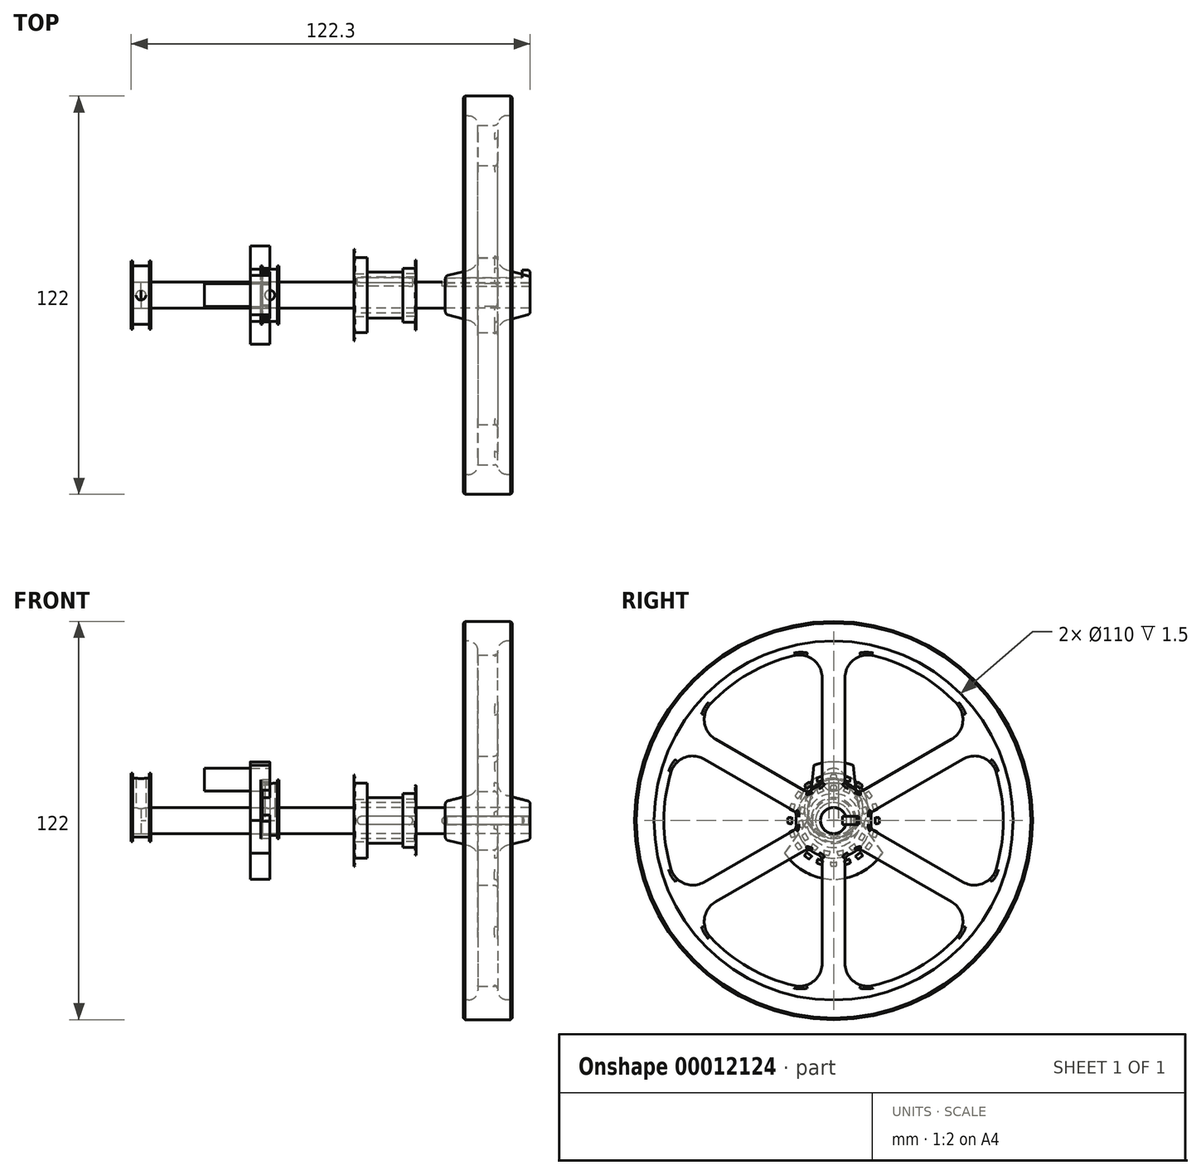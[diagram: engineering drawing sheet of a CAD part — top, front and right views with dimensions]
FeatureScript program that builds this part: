
annotation { "Feature Type Name" : "Feature", "Feature Type Description" : "" }
export const myFeature = defineFeature(function(context is Context, id is Id, definition is map)
    precondition{}
    {
        {
            var Q0;
            Q0=qCreatedBy(makeId("Right.planeOp"),FACE);
            var sketch = newSketch(context, id + "F0", { "sketchPlane" : qUnion([Q0])});
            skCircle(sketch, "E0", {"center": v(0, 0) * mm, "radius": 4 * mm});
            skSolve(sketch);
        }
        {
            var Q0;
            Q0=makeQuery(id+"F0.imprint","IMPRINT",FACE,{"disambiguationData":[TD([[makeQuery(id+"F0.imprint","IMPRINT",EDGE,{"derivedFrom":sQuery(id+"F0.wireOp",EDGE,"E0")}),1.0]])]});
            extrude(context, id + "F1", {"entities" : qUnion([Q0]), "oppositeDirection" : true, "depth" : 39.5 * mm});
        }
        {
            var Q0;
            Q0=makeQuery(id+"F1.opExtrude","CAP_FACE",FACE,{"disambiguationData":[OSD([sQuery(id+"F0.wireOp",EDGE,"E0")])],"isStart":true});
            var sketch = newSketch(context, id + "F2", { "sketchPlane" : qUnion([Q0])});
            skCircle(sketch, "E1", {"center": v(0, 0) * mm, "radius": 18 * mm});
            skLineSegment(sketch, "E2", {"start": v(0, 0) * mm, "end": v(0, 12.5) * mm, "construction": true});
            skCircle(sketch, "E3", {"center": v(0, 12.5) * mm, "radius": 3.5 * mm});
            skLineSegment(sketch, "E4.0", {"start": v(6, 0) * mm, "end": v(6, 16.97) * mm, "construction": true});
            skLineSegment(sketch, "E5", {"start": v(0, 0) * mm, "end": v(8, 0) * mm, "construction": true});
            skLineSegment(sketch, "E6", {"start": v(0, 0) * mm, "end": v(15, 0) * mm, "construction": true});
            skLineSegment(sketch, "E7", {"start": v(15, 0) * mm, "end": v(15, -9.95) * mm, "construction": true});
            skLineSegment(sketch, "E8", {"start": v(6, 16.97) * mm, "end": v(8, 0) * mm});
            skLineSegment(sketch, "E9", {"start": v(8, 0) * mm, "end": v(15, -9.95) * mm});
            skLineSegment(sketch, "E10.0.MirrorCS", {"start": v(-6, 16.97) * mm, "end": v(-8, 0) * mm});
            skLineSegment(sketch, "E11.0.MirrorCS", {"start": v(-8, 0) * mm, "end": v(-15, -9.95) * mm});
            skSolve(sketch);
        }
        {
            var Q0;
            Q0=makeQuery(id+"F2.imprint","IMPRINT",FACE,{"disambiguationData":[TD([[makeQuery(id+"F2.imprint","IMPRINT",EDGE,{"derivedFrom":sQuery(id+"F2.wireOp",EDGE,"E3")}),-1.0]])]});
            extrude(context, id + "F3", {"entities" : qUnion([Q0]), "oppositeDirection" : true, "depth" : 6 * mm});
        }
        {
            var Q0;
            Q0=makeQuery(id+"F2.imprint","IMPRINT",FACE,{"disambiguationData":[TD([[makeQuery(id+"F2.imprint","IMPRINT",EDGE,{"derivedFrom":sQuery(id+"F2.wireOp",EDGE,"E3")}),1.0]])]});
            extrude(context, id + "F4", {"entities" : qUnion([Q0]), "oppositeDirection" : true, "depth" : 20 * mm});
        }
        {
            var Q0;
            Q0=makeQuery(id+"F2.imprint","IMPRINT",FACE,{"disambiguationData":[TD([[makeQuery(id+"F2.imprint","IMPRINT",EDGE,{"derivedFrom":makeQuery(id+"F1.opExtrude","CAP_EDGE",EDGE,{"disambiguationData":[OSD([sQuery(id+"F0.wireOp",EDGE,"E0")])],"isStart":true})}),1.0]])]});
            extrude(context, id + "F5", {"entities" : qUnion([Q0]), "depth" : 79.8 * mm});
        }
        {
            var Q0;
            Q0=qCreatedBy(makeId("Front.planeOp"),FACE);
            cPlane(context, id + "F6", {"entities" : qUnion([Q0]), "cplaneType" : CPlaneType.OFFSET, "offset" : 4 * mm, "oppositeDirection" : true, "width" : 150 * mm, "height" : 150 * mm});
        }
        {
            var Q0;
            Q0=qCreatedBy(id+"F6.planeOp",FACE);
            var sketch = newSketch(context, id + "F7", { "sketchPlane" : qUnion([Q0])});
            skLineSegment(sketch, "E12.0", {"start": v(79.8, 4) * mm, "end": v(79.8, -4) * mm});
            skLineSegment(sketch, "E13", {"start": v(79.8, 0) * mm, "end": v(37.83, 0) * mm, "construction": true});
            skCircle(sketch, "E14", {"center": v(54.05, 0) * mm, "radius": 1.25 * mm});
            skCircle(sketch, "E15", {"center": v(42.55, 0) * mm, "radius": 1.25 * mm});
            skCircle(sketch, "E16", {"center": v(28.05, 0) * mm, "radius": 1.25 * mm});
            skLineSegment(sketch, "E17", {"start": v(54.05, -1.25) * mm, "end": v(79.8, -1.25) * mm});
            skLineSegment(sketch, "E18", {"start": v(42.55, 1.25) * mm, "end": v(28.05, 1.25) * mm});
            skLineSegment(sketch, "E19", {"start": v(42.55, -1.25) * mm, "end": v(28.05, -1.25) * mm});
            skLineSegment(sketch, "E20.0.MirrorCS", {"start": v(54.05, 1.25) * mm, "end": v(79.8, 1.25) * mm});
            skSolve(sketch);
        }
        {
            var Q0;
            {var subQ1=sQuery(id+"F7.wireOp",EDGE,"E17");Q0=makeQuery(id+"F7.imprint","IMPRINT",FACE,{"disambiguationData":[TD([[makeQuery(id+"F7.imprint","IMPRINT",EDGE,{"derivedFrom":subQ1}),1.0]])]});}
            var Q1;
            {var subQ0=sQuery(id+"F7.wireOp",EDGE,"E14");var subQ2=makeQuery(id+"F7.imprint","INTERSECT",VERTEX,{"derivedFrom":[subQ0,sQuery(id+"F7.wireOp",EDGE,"E17")]});Q1=makeQuery(id+"F7.imprint","IMPRINT",FACE,{"disambiguationData":[TD([[makeQuery(id+"F7.imprint","IMPRINT",EDGE,{"disambiguationData":[TD([[subQ2,1.0]])],"derivedFrom":subQ0}),1.0]])]});}
            var Q2;
            {var subQ1=sQuery(id+"F7.wireOp",EDGE,"E18");Q2=makeQuery(id+"F7.imprint","IMPRINT",FACE,{"disambiguationData":[TD([[makeQuery(id+"F7.imprint","IMPRINT",EDGE,{"derivedFrom":subQ1}),1.0]])]});}
            var Q3;
            {var subQ0=sQuery(id+"F7.wireOp",EDGE,"E15");var subQ2=makeQuery(id+"F7.imprint","INTERSECT",VERTEX,{"derivedFrom":[subQ0,sQuery(id+"F7.wireOp",EDGE,"E18")]});Q3=makeQuery(id+"F7.imprint","IMPRINT",FACE,{"disambiguationData":[TD([[makeQuery(id+"F7.imprint","IMPRINT",EDGE,{"disambiguationData":[TD([[subQ2,-1.0]])],"derivedFrom":subQ0}),1.0]])]});}
            var Q4;
            {var subQ0=sQuery(id+"F7.wireOp",EDGE,"E16");var subQ2=makeQuery(id+"F7.imprint","INTERSECT",VERTEX,{"derivedFrom":[subQ0,sQuery(id+"F7.wireOp",EDGE,"E18")]});Q4=makeQuery(id+"F7.imprint","IMPRINT",FACE,{"disambiguationData":[TD([[makeQuery(id+"F7.imprint","IMPRINT",EDGE,{"disambiguationData":[TD([[subQ2,-1.0]])],"derivedFrom":subQ0}),1.0]])]});}
            extrude(context, id + "F8", {"entities" : qUnion([Q0, Q1, Q2, Q3, Q4]), "operationType" : NewBodyOperationType.REMOVE, "depth" : 1.3 * mm});
        }
        {
            var Q0;
            Q0=qCreatedBy(makeId("Front.planeOp"),FACE);
            var sketch = newSketch(context, id + "F9", { "sketchPlane" : qUnion([Q0])});
            skLineSegment(sketch, "E21.0", {"start": v(79.8, 4) * mm, "end": v(79.8, -4) * mm});
            skLineSegment(sketch, "E22.bottom", {"start": v(79.8, 4) * mm, "end": v(53.8, 4) * mm});
            skLineSegment(sketch, "E22.top", {"start": v(79.8, 11.5) * mm, "end": v(53.8, 11.5) * mm});
            skLineSegment(sketch, "E22.left", {"start": v(79.8, 4) * mm, "end": v(79.8, 5.07) * mm});
            skLineSegment(sketch, "E22.right", {"start": v(53.8, 4) * mm, "end": v(53.8, 11.5) * mm});
            skLineSegment(sketch, "E23", {"start": v(66.8, 4) * mm, "end": v(66.8, 61) * mm, "construction": true});
            skLineSegment(sketch, "E24.bottom", {"start": v(74.3, 61) * mm, "end": v(59.3, 61) * mm});
            skLineSegment(sketch, "E24.top", {"start": v(74.3, 55) * mm, "end": v(72.8, 55) * mm});
            skLineSegment(sketch, "E24.left", {"start": v(74.3, 61) * mm, "end": v(74.3, 55) * mm});
            skLineSegment(sketch, "E24.right", {"start": v(59.3, 61) * mm, "end": v(59.3, 55) * mm});
            skLineSegment(sketch, "E25.bottom", {"start": v(60.8, 55) * mm, "end": v(59.3, 55) * mm});
            skLineSegment(sketch, "E25.top", {"start": v(69.8, 11.5) * mm, "end": v(63.8, 11.5) * mm});
            skLineSegment(sketch, "E25.left", {"start": v(69.8, 52) * mm, "end": v(69.8, 11.5) * mm});
            skLineSegment(sketch, "E25.right", {"start": v(63.8, 52) * mm, "end": v(63.8, 11.5) * mm});
            skArc(sketch, "E26.filletArc", {"start": v(72.8, 55) * mm, "mid": v(70.68, 54.12) * mm, "end": v(69.8, 52) * mm});
            skPoint(sketch, "E27.visualSharp", {"position": v(63.8, 55) * mm});
            skArc(sketch, "E27.filletArc", {"start": v(63.8, 52) * mm, "mid": v(62.92, 54.12) * mm, "end": v(60.8, 55) * mm});
            skLineSegment(sketch, "E28", {"start": v(79.05, 6.03) * mm, "end": v(72.81, 7.62) * mm});
            skLineSegment(sketch, "E29", {"start": v(69.8, 11.5) * mm, "end": v(69.8, 11.5) * mm});
            skPoint(sketch, "E30.visualSharp", {"position": v(69.8, 8.4) * mm});
            skArc(sketch, "E30.filletArc", {"start": v(69.8, 11.5) * mm, "mid": v(70.64, 9.05) * mm, "end": v(72.81, 7.62) * mm});
            skPoint(sketch, "E31.newPointB", {"position": v(79.8, 11.5) * mm});
            skArc(sketch, "E31.filletArc", {"start": v(79.8, 5.07) * mm, "mid": v(79.59, 5.68) * mm, "end": v(79.05, 6.03) * mm});
            skArc(sketch, "E32.0.MirrorCS", {"start": v(63.8, 11.5) * mm, "mid": v(62.96, 9.05) * mm, "end": v(60.79, 7.62) * mm});
            skLineSegment(sketch, "E33.0.MirrorCS", {"start": v(54.55, 6.03) * mm, "end": v(60.79, 7.62) * mm});
            skArc(sketch, "E34.0.MirrorCS", {"start": v(53.8, 5.07) * mm, "mid": v(54.01, 5.68) * mm, "end": v(54.55, 6.03) * mm});
            skLineSegment(sketch, "E35", {"start": v(79.8, 0) * mm, "end": v(85.65, 0) * mm, "construction": true});
            skSolve(sketch);
        }
        {
            var Q0;
            Q0=makeQuery(id+"F9.imprint","IMPRINT",FACE,{"disambiguationData":[TD([[makeQuery(id+"F9.imprint","IMPRINT",EDGE,{"derivedFrom":sQuery(id+"F9.wireOp",EDGE,"E24.bottom")}),1.0]])]});
            var Q1;
            {var subQ2=sQuery(id+"F9.wireOp",EDGE,"E22.bottom");Q1=makeQuery(id+"F9.imprint","IMPRINT",FACE,{"disambiguationData":[TD([[makeQuery(id+"F9.imprint","IMPRINT",EDGE,{"derivedFrom":subQ2}),-1.0]])]});}
            var Q2;
            Q2=sQuery(id+"F9.wireOp",EDGE,"E35");
            revolve(context, id + "F10", {"entities" : qUnion([Q0, Q1]), "axis" : qUnion([Q2]), "revolveType" : RevolveType.FULL});
        }
        {
            var Q0;
            Q0=makeQuery(id+"F10.opRevolve","SWEPT_FACE",FACE,{"disambiguationData":[OSD([sQuery(id+"F9.wireOp",EDGE,"E25.left")])]});
            var sketch = newSketch(context, id + "F11", { "sketchPlane" : qUnion([Q0])});
            skLineSegment(sketch, "E36", {"start": v(0, 0) * mm, "end": v(0, 52) * mm, "construction": true});
            skLineSegment(sketch, "E37.0", {"start": v(3.5, 0) * mm, "end": v(3.5, 52) * mm});
            skLineSegment(sketch, "E38.0.MirrorCS", {"start": v(-3.5, 0) * mm, "end": v(-3.5, 52) * mm});
            skLineSegment(sketch, "E39.1.0", {"start": v(-1.75, -3.03) * mm, "end": v(-46.78, 22.97) * mm});
            skLineSegment(sketch, "E39.1.1", {"start": v(1.75, 3.03) * mm, "end": v(-43.28, 29.03) * mm});
            skLineSegment(sketch, "E39.2.0", {"start": v(1.75, -3.03) * mm, "end": v(-43.28, -29.03) * mm});
            skLineSegment(sketch, "E39.2.1", {"start": v(-1.75, 3.03) * mm, "end": v(-46.78, -22.97) * mm});
            skLineSegment(sketch, "E39.3.0", {"start": v(3.5, 0) * mm, "end": v(3.5, -52) * mm});
            skLineSegment(sketch, "E39.3.1", {"start": v(-3.5, 0) * mm, "end": v(-3.5, -52) * mm});
            skLineSegment(sketch, "E39.4.0", {"start": v(1.75, 3.03) * mm, "end": v(46.78, -22.97) * mm});
            skLineSegment(sketch, "E39.4.1", {"start": v(-1.75, -3.03) * mm, "end": v(43.28, -29.03) * mm});
            skLineSegment(sketch, "E39.5.0", {"start": v(-1.75, 3.03) * mm, "end": v(43.28, 29.03) * mm});
            skLineSegment(sketch, "E39.5.1", {"start": v(1.75, -3.03) * mm, "end": v(46.78, 22.97) * mm});
            skPoint(sketch, "E39.center", {"position": v(0, 0) * mm});
            skCircle(sketch, "E40.0", {"center": v(0, 0) * mm, "radius": 52 * mm});
            skSolve(sketch);
        }
        {
            var Q0;
            {var subQ3=sQuery(id+"F11.wireOp",EDGE,"E38.0.MirrorCS");var subQ5=sQuery(id+"F11.wireOp",EDGE,"E40.0");var subQ7=makeQuery(id+"F11.imprint","INTERSECT",VERTEX,{"derivedFrom":[subQ3,subQ5]});Q0=makeQuery(id+"F11.imprint","IMPRINT",FACE,{"disambiguationData":[TD([[makeQuery(id+"F11.imprint","IMPRINT",EDGE,{"disambiguationData":[TD([[subQ7,1.0]])],"derivedFrom":subQ5}),-1.0]])]});}
            var Q1;
            {var subQ3=sQuery(id+"F11.wireOp",EDGE,"E37.0");var subQ5=sQuery(id+"F11.wireOp",EDGE,"E40.0");var subQ7=makeQuery(id+"F11.imprint","INTERSECT",VERTEX,{"derivedFrom":[subQ3,subQ5]});Q1=makeQuery(id+"F11.imprint","IMPRINT",FACE,{"disambiguationData":[TD([[makeQuery(id+"F11.imprint","IMPRINT",EDGE,{"disambiguationData":[TD([[subQ7,-1.0]])],"derivedFrom":subQ5}),-1.0]])]});}
            var Q2;
            {var subQ3=sQuery(id+"F11.wireOp",EDGE,"E39.4.0");var subQ5=sQuery(id+"F11.wireOp",EDGE,"E40.0");var subQ7=makeQuery(id+"F11.imprint","INTERSECT",VERTEX,{"derivedFrom":[subQ3,subQ5]});Q2=makeQuery(id+"F11.imprint","IMPRINT",FACE,{"disambiguationData":[TD([[makeQuery(id+"F11.imprint","IMPRINT",EDGE,{"disambiguationData":[TD([[subQ7,1.0]])],"derivedFrom":subQ5}),-1.0]])]});}
            var Q3;
            {var subQ3=sQuery(id+"F11.wireOp",EDGE,"E39.3.0");var subQ5=sQuery(id+"F11.wireOp",EDGE,"E40.0");var subQ7=makeQuery(id+"F11.imprint","INTERSECT",VERTEX,{"derivedFrom":[subQ3,subQ5]});Q3=makeQuery(id+"F11.imprint","IMPRINT",FACE,{"disambiguationData":[TD([[makeQuery(id+"F11.imprint","IMPRINT",EDGE,{"disambiguationData":[TD([[subQ7,1.0]])],"derivedFrom":subQ5}),-1.0]])]});}
            var Q4;
            {var subQ0=sQuery(id+"F11.wireOp",EDGE,"E40.0");var subQ3=sQuery(id+"F11.wireOp",EDGE,"E39.2.0");var subQ4=makeQuery(id+"F11.imprint","INTERSECT",VERTEX,{"derivedFrom":[subQ3,subQ0]});Q4=makeQuery(id+"F11.imprint","IMPRINT",FACE,{"disambiguationData":[TD([[makeQuery(id+"F11.imprint","IMPRINT",EDGE,{"disambiguationData":[TD([[subQ4,1.0]])],"derivedFrom":subQ0}),-1.0]])]});}
            var Q5;
            {var subQ3=sQuery(id+"F11.wireOp",EDGE,"E39.1.0");var subQ5=sQuery(id+"F11.wireOp",EDGE,"E40.0");var subQ7=makeQuery(id+"F11.imprint","INTERSECT",VERTEX,{"derivedFrom":[subQ3,subQ5]});Q5=makeQuery(id+"F11.imprint","IMPRINT",FACE,{"disambiguationData":[TD([[makeQuery(id+"F11.imprint","IMPRINT",EDGE,{"disambiguationData":[TD([[subQ7,1.0]])],"derivedFrom":subQ5}),-1.0]])]});}
            extrude(context, id + "F12", {"entities" : qUnion([Q0, Q1, Q2, Q3, Q4, Q5]), "operationType" : NewBodyOperationType.REMOVE, "oppositeDirection" : true, "depth" : 6 * mm});
        }
        {
            var Q0;
            Q0=makeQuery(id+"F12.boolean.opBoolean","COPY",EDGE,{"derivedFrom":makeQuery(id+"F12.opExtrude","SWEPT_EDGE",EDGE,{"disambiguationData":[OSD([sQuery(id+"F11.wireOp",EDGE,"E39.2.1"),sQuery(id+"F11.wireOp",EDGE,"E40.0")])]})});
            var Q1;
            Q1=makeQuery(id+"F12.boolean.opBoolean","COPY",EDGE,{"derivedFrom":makeQuery(id+"F12.opExtrude","SWEPT_EDGE",EDGE,{"disambiguationData":[OSD([sQuery(id+"F11.wireOp",EDGE,"E39.2.0"),sQuery(id+"F11.wireOp",EDGE,"E40.0")])]})});
            var Q2;
            Q2=makeQuery(id+"F12.boolean.opBoolean","COPY",EDGE,{"derivedFrom":makeQuery(id+"F12.opExtrude","SWEPT_EDGE",EDGE,{"disambiguationData":[OSD([sQuery(id+"F11.wireOp",EDGE,"E39.3.1"),sQuery(id+"F11.wireOp",EDGE,"E40.0")])]})});
            var Q3;
            Q3=makeQuery(id+"F12.boolean.opBoolean","COPY",EDGE,{"derivedFrom":makeQuery(id+"F12.opExtrude","SWEPT_EDGE",EDGE,{"disambiguationData":[OSD([sQuery(id+"F11.wireOp",EDGE,"E39.4.0"),sQuery(id+"F11.wireOp",EDGE,"E40.0")])]})});
            var Q4;
            Q4=makeQuery(id+"F12.boolean.opBoolean","COPY",EDGE,{"derivedFrom":makeQuery(id+"F12.opExtrude","SWEPT_EDGE",EDGE,{"disambiguationData":[OSD([sQuery(id+"F11.wireOp",EDGE,"E39.3.0"),sQuery(id+"F11.wireOp",EDGE,"E40.0")])]})});
            var Q5;
            Q5=makeQuery(id+"F12.boolean.opBoolean","COPY",EDGE,{"derivedFrom":makeQuery(id+"F12.opExtrude","SWEPT_EDGE",EDGE,{"disambiguationData":[OSD([sQuery(id+"F11.wireOp",EDGE,"E39.4.1"),sQuery(id+"F11.wireOp",EDGE,"E40.0")])]})});
            var Q6;
            Q6=makeQuery(id+"F12.boolean.opBoolean","COPY",EDGE,{"derivedFrom":makeQuery(id+"F12.opExtrude","SWEPT_EDGE",EDGE,{"disambiguationData":[OSD([sQuery(id+"F11.wireOp",EDGE,"E39.5.1"),sQuery(id+"F11.wireOp",EDGE,"E40.0")])]})});
            var Q7;
            Q7=makeQuery(id+"F12.boolean.opBoolean","COPY",EDGE,{"derivedFrom":makeQuery(id+"F12.opExtrude","SWEPT_EDGE",EDGE,{"disambiguationData":[OSD([sQuery(id+"F11.wireOp",EDGE,"E39.5.0"),sQuery(id+"F11.wireOp",EDGE,"E40.0")])]})});
            var Q8;
            Q8=makeQuery(id+"F12.boolean.opBoolean","COPY",EDGE,{"derivedFrom":makeQuery(id+"F12.opExtrude","SWEPT_EDGE",EDGE,{"disambiguationData":[OSD([sQuery(id+"F11.wireOp",EDGE,"E38.0.MirrorCS"),sQuery(id+"F11.wireOp",EDGE,"E40.0")])]})});
            var Q9;
            Q9=makeQuery(id+"F12.boolean.opBoolean","COPY",EDGE,{"derivedFrom":makeQuery(id+"F12.opExtrude","SWEPT_EDGE",EDGE,{"disambiguationData":[OSD([sQuery(id+"F11.wireOp",EDGE,"E37.0"),sQuery(id+"F11.wireOp",EDGE,"E40.0")])]})});
            var Q10;
            Q10=makeQuery(id+"F12.boolean.opBoolean","COPY",EDGE,{"derivedFrom":makeQuery(id+"F12.opExtrude","SWEPT_EDGE",EDGE,{"disambiguationData":[OSD([sQuery(id+"F11.wireOp",EDGE,"E39.1.0"),sQuery(id+"F11.wireOp",EDGE,"E40.0")])]})});
            var Q11;
            Q11=makeQuery(id+"F12.boolean.opBoolean","COPY",EDGE,{"derivedFrom":makeQuery(id+"F12.opExtrude","SWEPT_EDGE",EDGE,{"disambiguationData":[OSD([sQuery(id+"F11.wireOp",EDGE,"E39.1.1"),sQuery(id+"F11.wireOp",EDGE,"E40.0")])]})});
            fillet(context, id + "F13", {"entities" : qUnion([Q0, Q1, Q2, Q3, Q4, Q5, Q6, Q7, Q8, Q9, Q10, Q11]), "radius" : 7 * mm, "tangentPropagation" : true, "allowEdgeOverflow" : false});
        }
        {
            var Q0;
            Q0=makeQuery(id+"F12.boolean.opBoolean","COPY",EDGE,{"derivedFrom":makeQuery(id+"F12.opExtrude","SWEPT_EDGE",EDGE,{"disambiguationData":[OSD([sQuery(id+"F9.wireOp",EDGE,"E25.top"),sQuery(id+"F9.wireOp",EDGE,"E25.left"),sQuery(id+"F9.wireOp",EDGE,"E30.filletArc"),sQuery(id+"F11.wireOp",EDGE,"E39.4.0")])]})});
            var Q1;
            Q1=makeQuery(id+"F12.boolean.opBoolean","COPY",EDGE,{"derivedFrom":makeQuery(id+"F12.opExtrude","SWEPT_EDGE",EDGE,{"disambiguationData":[OSD([sQuery(id+"F9.wireOp",EDGE,"E25.top"),sQuery(id+"F9.wireOp",EDGE,"E25.left"),sQuery(id+"F9.wireOp",EDGE,"E30.filletArc"),sQuery(id+"F11.wireOp",EDGE,"E39.5.1")])]})});
            var Q2;
            Q2=makeQuery(id+"F12.boolean.opBoolean","COPY",EDGE,{"derivedFrom":makeQuery(id+"F12.opExtrude","SWEPT_EDGE",EDGE,{"disambiguationData":[OSD([sQuery(id+"F9.wireOp",EDGE,"E25.top"),sQuery(id+"F9.wireOp",EDGE,"E25.left"),sQuery(id+"F9.wireOp",EDGE,"E30.filletArc"),sQuery(id+"F11.wireOp",EDGE,"E37.0")])]})});
            var Q3;
            Q3=makeQuery(id+"F12.boolean.opBoolean","COPY",EDGE,{"derivedFrom":makeQuery(id+"F12.opExtrude","SWEPT_EDGE",EDGE,{"disambiguationData":[OSD([sQuery(id+"F9.wireOp",EDGE,"E25.top"),sQuery(id+"F9.wireOp",EDGE,"E25.left"),sQuery(id+"F9.wireOp",EDGE,"E30.filletArc"),sQuery(id+"F11.wireOp",EDGE,"E39.5.0")])]})});
            var Q4;
            Q4=makeQuery(id+"F12.boolean.opBoolean","COPY",EDGE,{"derivedFrom":makeQuery(id+"F12.opExtrude","SWEPT_EDGE",EDGE,{"disambiguationData":[OSD([sQuery(id+"F9.wireOp",EDGE,"E25.top"),sQuery(id+"F9.wireOp",EDGE,"E25.left"),sQuery(id+"F9.wireOp",EDGE,"E30.filletArc"),sQuery(id+"F11.wireOp",EDGE,"E38.0.MirrorCS")])]})});
            var Q5;
            Q5=makeQuery(id+"F12.boolean.opBoolean","COPY",EDGE,{"derivedFrom":makeQuery(id+"F12.opExtrude","SWEPT_EDGE",EDGE,{"disambiguationData":[OSD([sQuery(id+"F9.wireOp",EDGE,"E25.top"),sQuery(id+"F9.wireOp",EDGE,"E25.left"),sQuery(id+"F9.wireOp",EDGE,"E30.filletArc"),sQuery(id+"F11.wireOp",EDGE,"E39.1.1")])]})});
            var Q6;
            Q6=makeQuery(id+"F12.boolean.opBoolean","COPY",EDGE,{"derivedFrom":makeQuery(id+"F12.opExtrude","SWEPT_EDGE",EDGE,{"disambiguationData":[OSD([sQuery(id+"F9.wireOp",EDGE,"E25.top"),sQuery(id+"F9.wireOp",EDGE,"E25.left"),sQuery(id+"F9.wireOp",EDGE,"E30.filletArc"),sQuery(id+"F11.wireOp",EDGE,"E39.1.0")])]})});
            var Q7;
            Q7=makeQuery(id+"F12.boolean.opBoolean","COPY",EDGE,{"derivedFrom":makeQuery(id+"F12.opExtrude","SWEPT_EDGE",EDGE,{"disambiguationData":[OSD([sQuery(id+"F9.wireOp",EDGE,"E25.top"),sQuery(id+"F9.wireOp",EDGE,"E25.left"),sQuery(id+"F9.wireOp",EDGE,"E30.filletArc"),sQuery(id+"F11.wireOp",EDGE,"E39.2.1")])]})});
            var Q8;
            Q8=makeQuery(id+"F12.boolean.opBoolean","COPY",EDGE,{"derivedFrom":makeQuery(id+"F12.opExtrude","SWEPT_EDGE",EDGE,{"disambiguationData":[OSD([sQuery(id+"F9.wireOp",EDGE,"E25.top"),sQuery(id+"F9.wireOp",EDGE,"E25.left"),sQuery(id+"F9.wireOp",EDGE,"E30.filletArc"),sQuery(id+"F11.wireOp",EDGE,"E39.2.0")])]})});
            var Q9;
            Q9=makeQuery(id+"F12.boolean.opBoolean","COPY",EDGE,{"derivedFrom":makeQuery(id+"F12.opExtrude","SWEPT_EDGE",EDGE,{"disambiguationData":[OSD([sQuery(id+"F9.wireOp",EDGE,"E25.top"),sQuery(id+"F9.wireOp",EDGE,"E25.left"),sQuery(id+"F9.wireOp",EDGE,"E30.filletArc"),sQuery(id+"F11.wireOp",EDGE,"E39.3.1")])]})});
            var Q10;
            Q10=makeQuery(id+"F12.boolean.opBoolean","COPY",EDGE,{"derivedFrom":makeQuery(id+"F12.opExtrude","SWEPT_EDGE",EDGE,{"disambiguationData":[OSD([sQuery(id+"F9.wireOp",EDGE,"E25.top"),sQuery(id+"F9.wireOp",EDGE,"E25.left"),sQuery(id+"F9.wireOp",EDGE,"E30.filletArc"),sQuery(id+"F11.wireOp",EDGE,"E39.3.0")])]})});
            var Q11;
            Q11=makeQuery(id+"F12.boolean.opBoolean","COPY",EDGE,{"derivedFrom":makeQuery(id+"F12.opExtrude","SWEPT_EDGE",EDGE,{"disambiguationData":[OSD([sQuery(id+"F9.wireOp",EDGE,"E25.top"),sQuery(id+"F9.wireOp",EDGE,"E25.left"),sQuery(id+"F9.wireOp",EDGE,"E30.filletArc"),sQuery(id+"F11.wireOp",EDGE,"E39.4.1")])]})});
            fillet(context, id + "F14", {"entities" : qUnion([Q0, Q1, Q2, Q3, Q4, Q5, Q6, Q7, Q8, Q9, Q10, Q11]), "radius" : 2 * mm, "tangentPropagation" : true, "allowEdgeOverflow" : false});
        }
        {
            var Q0;
            {var subQ0=sQuery(id+"F9.wireOp",EDGE,"E25.top");var subQ1=sQuery(id+"F9.wireOp",EDGE,"E25.left");var subQ2=sQuery(id+"F9.wireOp",EDGE,"E30.filletArc");var subQ3=makeQuery(id+"F10.opRevolve","SWEPT_EDGE",EDGE,{"disambiguationData":[OSD([subQ0,subQ1,subQ2])]});Q0=makeQuery(id+"F12.boolean.opBoolean","MERGE",EDGE,{"derivedFrom":[subQ3,makeQuery(id+"F12.opExtrude","CAP_EDGE",EDGE,{"disambiguationData":[OSD([subQ0,subQ1,subQ2]),TDD([makeQuery(id+"F11.imprint","IMPRINT",EDGE,{"disambiguationData":[TD([[makeQuery(id+"F11.imprint","INTERSECT",VERTEX,{"derivedFrom":[subQ3,sQuery(id+"F11.wireOp",EDGE,"E38.0.MirrorCS")]}),1.0]])],"derivedFrom":subQ3})])],"isStart":true})]});}
            var Q1;
            {var subQ0=sQuery(id+"F9.wireOp",EDGE,"E25.top");var subQ1=sQuery(id+"F9.wireOp",EDGE,"E25.left");var subQ2=sQuery(id+"F9.wireOp",EDGE,"E30.filletArc");var subQ3=makeQuery(id+"F10.opRevolve","SWEPT_EDGE",EDGE,{"disambiguationData":[OSD([subQ0,subQ1,subQ2])]});Q1=makeQuery(id+"F12.boolean.opBoolean","MERGE",EDGE,{"derivedFrom":[subQ3,makeQuery(id+"F12.opExtrude","CAP_EDGE",EDGE,{"disambiguationData":[OSD([subQ0,subQ1,subQ2]),TDD([makeQuery(id+"F11.imprint","IMPRINT",EDGE,{"disambiguationData":[TD([[makeQuery(id+"F11.imprint","INTERSECT",VERTEX,{"derivedFrom":[subQ3,sQuery(id+"F11.wireOp",EDGE,"E37.0")]}),-1.0]])],"derivedFrom":subQ3})])],"isStart":true})]});}
            var Q2;
            {var subQ0=sQuery(id+"F9.wireOp",EDGE,"E25.top");var subQ1=sQuery(id+"F9.wireOp",EDGE,"E25.left");var subQ2=sQuery(id+"F9.wireOp",EDGE,"E30.filletArc");var subQ3=makeQuery(id+"F10.opRevolve","SWEPT_EDGE",EDGE,{"disambiguationData":[OSD([subQ0,subQ1,subQ2])]});Q2=makeQuery(id+"F12.boolean.opBoolean","MERGE",EDGE,{"derivedFrom":[subQ3,makeQuery(id+"F12.opExtrude","CAP_EDGE",EDGE,{"disambiguationData":[OSD([subQ0,subQ1,subQ2]),TDD([makeQuery(id+"F11.imprint","IMPRINT",EDGE,{"disambiguationData":[TD([[makeQuery(id+"F11.imprint","INTERSECT",VERTEX,{"derivedFrom":[subQ3,sQuery(id+"F11.wireOp",EDGE,"E39.4.0")]}),1.0]])],"derivedFrom":subQ3})])],"isStart":true})]});}
            var Q3;
            {var subQ0=sQuery(id+"F9.wireOp",EDGE,"E25.top");var subQ1=sQuery(id+"F9.wireOp",EDGE,"E25.left");var subQ2=sQuery(id+"F9.wireOp",EDGE,"E30.filletArc");var subQ3=makeQuery(id+"F10.opRevolve","SWEPT_EDGE",EDGE,{"disambiguationData":[OSD([subQ0,subQ1,subQ2])]});Q3=makeQuery(id+"F12.boolean.opBoolean","MERGE",EDGE,{"derivedFrom":[subQ3,makeQuery(id+"F12.opExtrude","CAP_EDGE",EDGE,{"disambiguationData":[OSD([subQ0,subQ1,subQ2]),TDD([makeQuery(id+"F11.imprint","IMPRINT",EDGE,{"disambiguationData":[TD([[makeQuery(id+"F11.imprint","INTERSECT",VERTEX,{"derivedFrom":[subQ3,sQuery(id+"F11.wireOp",EDGE,"E39.1.0")]}),1.0]])],"derivedFrom":subQ3})])],"isStart":true})]});}
            var Q4;
            {var subQ0=sQuery(id+"F9.wireOp",EDGE,"E25.top");var subQ1=sQuery(id+"F9.wireOp",EDGE,"E25.left");var subQ2=sQuery(id+"F9.wireOp",EDGE,"E30.filletArc");var subQ3=makeQuery(id+"F10.opRevolve","SWEPT_EDGE",EDGE,{"disambiguationData":[OSD([subQ0,subQ1,subQ2])]});Q4=makeQuery(id+"F12.boolean.opBoolean","MERGE",EDGE,{"derivedFrom":[subQ3,makeQuery(id+"F12.opExtrude","CAP_EDGE",EDGE,{"disambiguationData":[OSD([subQ0,subQ1,subQ2]),TDD([makeQuery(id+"F11.imprint","IMPRINT",EDGE,{"disambiguationData":[TD([[makeQuery(id+"F11.imprint","INTERSECT",VERTEX,{"derivedFrom":[subQ3,sQuery(id+"F11.wireOp",EDGE,"E39.2.0")]}),1.0]])],"derivedFrom":subQ3})])],"isStart":true})]});}
            var Q5;
            {var subQ0=sQuery(id+"F9.wireOp",EDGE,"E25.top");var subQ1=sQuery(id+"F9.wireOp",EDGE,"E25.left");var subQ2=sQuery(id+"F9.wireOp",EDGE,"E30.filletArc");var subQ3=makeQuery(id+"F10.opRevolve","SWEPT_EDGE",EDGE,{"disambiguationData":[OSD([subQ0,subQ1,subQ2])]});Q5=makeQuery(id+"F12.boolean.opBoolean","MERGE",EDGE,{"derivedFrom":[subQ3,makeQuery(id+"F12.opExtrude","CAP_EDGE",EDGE,{"disambiguationData":[OSD([subQ0,subQ1,subQ2]),TDD([makeQuery(id+"F11.imprint","IMPRINT",EDGE,{"disambiguationData":[TD([[makeQuery(id+"F11.imprint","INTERSECT",VERTEX,{"derivedFrom":[subQ3,sQuery(id+"F11.wireOp",EDGE,"E39.3.0")]}),1.0]])],"derivedFrom":subQ3})])],"isStart":true})]});}
            var Q6;
            Q6=makeQuery(id+"F12.boolean.opBoolean","COPY",EDGE,{"derivedFrom":makeQuery(id+"F12.opExtrude","CAP_EDGE",EDGE,{"disambiguationData":[OSD([sQuery(id+"F11.wireOp",EDGE,"E39.1.1")])],"isStart":true})});
            var Q7;
            Q7=makeQuery(id+"F12.boolean.opBoolean","COPY",EDGE,{"derivedFrom":makeQuery(id+"F12.opExtrude","CAP_EDGE",EDGE,{"disambiguationData":[OSD([sQuery(id+"F11.wireOp",EDGE,"E39.1.1")])],"isStart":false})});
            var Q8;
            Q8=makeQuery(id+"F12.boolean.opBoolean","COPY",EDGE,{"derivedFrom":makeQuery(id+"F12.opExtrude","CAP_EDGE",EDGE,{"disambiguationData":[OSD([sQuery(id+"F11.wireOp",EDGE,"E39.2.1")])],"isStart":false})});
            var Q9;
            Q9=makeQuery(id+"F12.boolean.opBoolean","COPY",EDGE,{"derivedFrom":makeQuery(id+"F12.opExtrude","CAP_EDGE",EDGE,{"disambiguationData":[OSD([sQuery(id+"F11.wireOp",EDGE,"E39.2.0")])],"isStart":false})});
            var Q10;
            Q10=makeQuery(id+"F12.boolean.opBoolean","COPY",EDGE,{"derivedFrom":makeQuery(id+"F12.opExtrude","CAP_EDGE",EDGE,{"disambiguationData":[OSD([sQuery(id+"F11.wireOp",EDGE,"E39.5.0")])],"isStart":false})});
            var Q11;
            Q11=makeQuery(id+"F12.boolean.opBoolean","COPY",EDGE,{"derivedFrom":makeQuery(id+"F12.opExtrude","CAP_EDGE",EDGE,{"disambiguationData":[OSD([sQuery(id+"F11.wireOp",EDGE,"E39.4.0")])],"isStart":false})});
            var Q12;
            Q12=makeQuery(id+"F12.boolean.opBoolean","COPY",EDGE,{"derivedFrom":makeQuery(id+"F12.opExtrude","CAP_EDGE",EDGE,{"disambiguationData":[OSD([sQuery(id+"F11.wireOp",EDGE,"E39.3.0")])],"isStart":false})});
            fillet(context, id + "F15", {"entities" : qUnion([Q0, Q1, Q2, Q3, Q4, Q5, Q6, Q7, Q8, Q9, Q10, Q11, Q12]), "radius" : 1 * mm, "tangentPropagation" : true, "allowEdgeOverflow" : false});
        }
        {
            var Q0;
            Q0=makeQuery(id+"F10.opRevolve","SWEPT_EDGE",EDGE,{"disambiguationData":[OSD([sQuery(id+"F9.wireOp",EDGE,"E24.bottom"),sQuery(id+"F9.wireOp",EDGE,"E24.left")])]});
            var Q1;
            Q1=makeQuery(id+"F10.opRevolve","SWEPT_EDGE",EDGE,{"disambiguationData":[OSD([sQuery(id+"F9.wireOp",EDGE,"E24.bottom"),sQuery(id+"F9.wireOp",EDGE,"E24.right")])]});
            chamfer(context, id + "F16", {"entities" : qUnion([Q0, Q1]), "width" : 0.5 * mm, "tangentPropagation" : true});
        }
        {
            var Q0;
            Q0=makeQuery(id+"F10.opRevolve","SWEPT_FACE",FACE,{"disambiguationData":[OSD([sQuery(id+"F9.wireOp",EDGE,"E22.left")])]});
            var sketch = newSketch(context, id + "F17", { "sketchPlane" : qUnion([Q0])});
            skLineSegment(sketch, "E41.0", {"start": v(2.7, 1.25) * mm, "end": v(3.8, 1.25) * mm});
            skLineSegment(sketch, "E41.1", {"start": v(2.7, -1.25) * mm, "end": v(3.8, -1.25) * mm});
            skLineSegment(sketch, "E42", {"start": v(3.8, 1.25) * mm, "end": v(6.32, 1.25) * mm});
            skLineSegment(sketch, "E43", {"start": v(6.32, 1.25) * mm, "end": v(6.32, -1.25) * mm});
            skLineSegment(sketch, "E44", {"start": v(6.32, -1.25) * mm, "end": v(3.8, -1.25) * mm});
            skLineSegment(sketch, "E45", {"start": v(2.7, 1.25) * mm, "end": v(2.7, -1.25) * mm});
            skLineSegment(sketch, "E46", {"start": v(5.3, 1.25) * mm, "end": v(5.3, -1.25) * mm});
            skSolve(sketch);
        }
        {
            var Q0;
            {var subQ0=sQuery(id+"F9.wireOp",EDGE,"E22.left");var subQ4=sQuery(id+"F17.wireOp",EDGE,"E42");var subQ6=makeQuery(id+"F10.opRevolve","SWEPT_EDGE",EDGE,{"disambiguationData":[OSD([subQ0,sQuery(id+"F9.wireOp",EDGE,"E31.filletArc")])]});var subQ8=makeQuery(id+"F17.imprint","INTERSECT",VERTEX,{"derivedFrom":[subQ6,subQ4]});Q0=makeQuery(id+"F17.imprint","IMPRINT",FACE,{"disambiguationData":[TD([[makeQuery(id+"F17.imprint","IMPRINT",EDGE,{"disambiguationData":[TD([[subQ8,1.0]])],"derivedFrom":subQ4}),-1.0]])]});}
            var Q1;
            {var subQ2=sQuery(id+"F17.wireOp",EDGE,"E43");Q1=makeQuery(id+"F17.imprint","IMPRINT",FACE,{"disambiguationData":[TD([[makeQuery(id+"F17.imprint","IMPRINT",EDGE,{"derivedFrom":subQ2}),-1.0]])]});}
            var Q2;
            {var subQ5=sQuery(id+"F17.wireOp",EDGE,"E46");Q2=makeQuery(id+"F17.imprint","IMPRINT",FACE,{"disambiguationData":[TD([[makeQuery(id+"F17.imprint","IMPRINT",EDGE,{"derivedFrom":subQ5}),-1.0]])]});}
            extrude(context, id + "F18", {"entities" : qUnion([Q0, Q1, Q2]), "operationType" : NewBodyOperationType.REMOVE, "oppositeDirection" : true, "depth" : 2.5 * mm});
        }
        {
            var Q0;
            {var subQ0=sQuery(id+"F9.wireOp",EDGE,"E22.left");var subQ4=sQuery(id+"F17.wireOp",EDGE,"E42");var subQ6=makeQuery(id+"F10.opRevolve","SWEPT_EDGE",EDGE,{"disambiguationData":[OSD([subQ0,sQuery(id+"F9.wireOp",EDGE,"E31.filletArc")])]});var subQ8=makeQuery(id+"F17.imprint","INTERSECT",VERTEX,{"derivedFrom":[subQ6,subQ4]});Q0=makeQuery(id+"F17.imprint","IMPRINT",FACE,{"disambiguationData":[TD([[makeQuery(id+"F17.imprint","IMPRINT",EDGE,{"disambiguationData":[TD([[subQ8,1.0]])],"derivedFrom":subQ4}),-1.0]])]});}
            var Q1;
            {var subQ5=sQuery(id+"F17.wireOp",EDGE,"E46");Q1=makeQuery(id+"F17.imprint","IMPRINT",FACE,{"disambiguationData":[TD([[makeQuery(id+"F17.imprint","IMPRINT",EDGE,{"derivedFrom":subQ5}),-1.0]])]});}
            extrude(context, id + "F19", {"entities" : qUnion([Q0, Q1]), "operationType" : NewBodyOperationType.REMOVE, "oppositeDirection" : true, "depth" : 26 * mm});
        }
        {
            var Q0;
            Q0=makeQuery(id+"F8.boolean.opBoolean","COPY",FACE,{"derivedFrom":makeQuery(id+"F8.opExtrude","SWEPT_FACE",FACE,{"disambiguationData":[OSD([sQuery(id+"F7.wireOp",EDGE,"E17")])]})});
            var sketch = newSketch(context, id + "F20", { "sketchPlane" : qUnion([Q0])});
            skLineSegment(sketch, "E47", {"start": v(79.8, 2.7) * mm, "end": v(79.8, 7.7) * mm});
            skLineSegment(sketch, "E48", {"start": v(79.8, 7.7) * mm, "end": v(77.3, 7.7) * mm});
            skLineSegment(sketch, "E49", {"start": v(77.3, 7.7) * mm, "end": v(77.3, 5.4) * mm});
            skLineSegment(sketch, "E50", {"start": v(77.3, 5.4) * mm, "end": v(54.3, 5.2) * mm});
            skLineSegment(sketch, "E51", {"start": v(54.3, 5.2) * mm, "end": v(54.3, 2.7) * mm});
            skLineSegment(sketch, "E52", {"start": v(54.3, 2.7) * mm, "end": v(79.8, 2.7) * mm});
            skSolve(sketch);
        }
        {
            var Q0;
            {var subQ6=sQuery(id+"F20.wireOp",EDGE,"E48");Q0=makeQuery(id+"F20.imprint","IMPRINT",FACE,{"disambiguationData":[TD([[makeQuery(id+"F20.imprint","IMPRINT",EDGE,{"derivedFrom":subQ6}),1.0]])]});}
            var Q1;
            {var subQ6=sQuery(id+"F20.wireOp",EDGE,"E52");Q1=makeQuery(id+"F20.imprint","IMPRINT",FACE,{"disambiguationData":[TD([[makeQuery(id+"F20.imprint","IMPRINT",EDGE,{"derivedFrom":subQ6}),1.0]])]});}
            extrude(context, id + "F21", {"entities" : qUnion([Q0, Q1]), "depth" : 2.5 * mm});
        }
        {
            var Q0;
            Q0=makeQuery(id+"F21.opExtrude","SWEPT_EDGE",EDGE,{"disambiguationData":[OSD([sQuery(id+"F20.wireOp",EDGE,"E47"),sQuery(id+"F20.wireOp",EDGE,"E48")])]});
            chamfer(context, id + "F22", {"entities" : qUnion([Q0]), "width" : 0.5 * mm, "tangentPropagation" : true});
        }
        {
            var Q0;
            {var subQ1=sQuery(id+"F7.wireOp",EDGE,"E18");Q0=makeQuery(id+"F7.imprint","IMPRINT",FACE,{"disambiguationData":[TD([[makeQuery(id+"F7.imprint","IMPRINT",EDGE,{"derivedFrom":subQ1}),1.0]])]});}
            var Q1;
            {var subQ0=sQuery(id+"F7.wireOp",EDGE,"E15");var subQ2=makeQuery(id+"F7.imprint","INTERSECT",VERTEX,{"derivedFrom":[subQ0,sQuery(id+"F7.wireOp",EDGE,"E18")]});Q1=makeQuery(id+"F7.imprint","IMPRINT",FACE,{"disambiguationData":[TD([[makeQuery(id+"F7.imprint","IMPRINT",EDGE,{"disambiguationData":[TD([[subQ2,-1.0]])],"derivedFrom":subQ0}),1.0]])]});}
            var Q2;
            {var subQ0=sQuery(id+"F7.wireOp",EDGE,"E16");var subQ2=makeQuery(id+"F7.imprint","INTERSECT",VERTEX,{"derivedFrom":[subQ0,sQuery(id+"F7.wireOp",EDGE,"E18")]});Q2=makeQuery(id+"F7.imprint","IMPRINT",FACE,{"disambiguationData":[TD([[makeQuery(id+"F7.imprint","IMPRINT",EDGE,{"disambiguationData":[TD([[subQ2,-1.0]])],"derivedFrom":subQ0}),1.0]])]});}
            extrude(context, id + "F23", {"entities" : qUnion([Q0, Q1, Q2]), "depth" : 2.5 * mm, "symmetric" : true});
        }
        {
            var Q0;
            Q0=makeQuery(id+"F5.opExtrude","CAP_FACE",FACE,{"disambiguationData":[OSD([sQuery(id+"F0.wireOp",EDGE,"E0")])],"isStart":false});
            cPlane(context, id + "F24", {"entities" : qUnion([Q0]), "cplaneType" : CPlaneType.OFFSET, "offset" : (27 + 9 + 8.5) * mm, "oppositeDirection" : true, "width" : 150 * mm, "height" : 150 * mm});
        }
        {
            var Q0;
            Q0=qCreatedBy(id+"F24.planeOp",FACE);
            var sketch = newSketch(context, id + "F25", { "sketchPlane" : qUnion([Q0])});
            skCircle(sketch, "E53", {"center": v(0, 0) * mm, "radius": 5.5 * mm});
            skLineSegment(sketch, "E54.0", {"start": v(2.75, 1.25) * mm, "end": v(5.36, 1.25) * mm});
            skLineSegment(sketch, "E54.1", {"start": v(2.75, -1.25) * mm, "end": v(5.36, -1.25) * mm});
            skPoint(sketch, "E55.orphan", {"position": v(5.25, 1.25) * mm});
            skPoint(sketch, "E56.orphan", {"position": v(5.25, -1.25) * mm});
            skCircle(sketch, "E57.0", {"center": v(0, 0) * mm, "radius": 4 * mm});
            skSolve(sketch);
        }
        {
            var Q0;
            {var subQ3=sQuery(id+"F25.wireOp",EDGE,"E54.0");var subQ5=sQuery(id+"F25.wireOp",EDGE,"E53");var subQ7=makeQuery(id+"F25.imprint","INTERSECT",VERTEX,{"derivedFrom":[subQ5,subQ3]});Q0=makeQuery(id+"F25.imprint","IMPRINT",FACE,{"disambiguationData":[TD([[makeQuery(id+"F25.imprint","IMPRINT",EDGE,{"disambiguationData":[TD([[subQ7,-1.0]])],"derivedFrom":subQ5}),1.0]])]});}
            extrude(context, id + "F26", {"entities" : qUnion([Q0]), "depth" : 19 * mm, "symmetric" : true});
        }
        {
            var Q0;
            Q0=qCreatedBy(id+"F24.planeOp",FACE);
            var sketch = newSketch(context, id + "F27", { "sketchPlane" : qUnion([Q0])});
            skArc(sketch, "E58.0", {"start": v(5.36, 1.25) * mm, "mid": v(-5.5, 0) * mm, "end": v(5.36, -1.25) * mm});
            skCircle(sketch, "E59", {"center": v(0, 0) * mm, "radius": 6.5 * mm});
            skCircle(sketch, "E60", {"center": v(0, 0) * mm, "radius": 7 * mm});
            skCircle(sketch, "E61.0", {"center": v(0, 0) * mm, "radius": 4 * mm});
            skCircle(sketch, "E62", {"center": v(0, 0) * mm, "radius": 5.5 * mm});
            skSolve(sketch);
        }
        {
            var Q0;
            Q0=makeQuery(id+"F27.imprint","IMPRINT",FACE,{"disambiguationData":[TD([[makeQuery(id+"F27.imprint","IMPRINT",EDGE,{"derivedFrom":sQuery(id+"F27.wireOp",EDGE,"E59")}),1.0]])]});
            extrude(context, id + "F28", {"entities" : qUnion([Q0]), "depth" : 19 * mm, "symmetric" : true});
        }
        {
            var Q0;
            Q0=makeQuery(id+"F27.imprint","IMPRINT",FACE,{"disambiguationData":[TD([[makeQuery(id+"F27.imprint","IMPRINT",EDGE,{"derivedFrom":sQuery(id+"F27.wireOp",EDGE,"E59")}),-1.0]])]});
            extrude(context, id + "F29", {"entities" : qUnion([Q0]), "operationType" : NewBodyOperationType.ADD, "depth" : 11 * mm, "symmetric" : true});
        }
        {
            var Q0;
            Q0=makeQuery(id+"F5.opExtrude","CAP_FACE",FACE,{"disambiguationData":[OSD([sQuery(id+"F0.wireOp",EDGE,"E0")])],"isStart":true});
            var sketch = newSketch(context, id + "F30", { "sketchPlane" : qUnion([Q0])});
            skLineSegment(sketch, "E63", {"start": v(0, 0) * mm, "end": v(0, 3.5) * mm, "construction": true});
            skCircle(sketch, "E64", {"center": v(0, 3.5) * mm, "radius": 9 * mm});
            skCircle(sketch, "E65", {"center": v(0, 3.5) * mm, "radius": 8 * mm});
            skSolve(sketch);
        }
        {
            var Q0;
            Q0=makeQuery(id+"F30.imprint","IMPRINT",FACE,{"disambiguationData":[TD([[makeQuery(id+"F30.imprint","IMPRINT",EDGE,{"derivedFrom":sQuery(id+"F30.wireOp",EDGE,"E65")}),1.0]])]});
            var Q1;
            Q1=makeQuery(id+"F30.imprint","IMPRINT",FACE,{"disambiguationData":[TD([[makeQuery(id+"F30.imprint","IMPRINT",EDGE,{"derivedFrom":sQuery(id+"F30.wireOp",EDGE,"E64")}),1.0]])]});
            extrude(context, id + "F31", {"entities" : qUnion([Q0, Q1]), "depth" : 5.5 * mm, "symmetric" : true});
        }
        {
            var Q0;
            Q0=makeQuery(id+"F30.imprint","IMPRINT",FACE,{"disambiguationData":[TD([[makeQuery(id+"F30.imprint","IMPRINT",EDGE,{"derivedFrom":sQuery(id+"F30.wireOp",EDGE,"E64")}),1.0]])]});
            extrude(context, id + "F32", {"entities" : qUnion([Q0]), "operationType" : NewBodyOperationType.REMOVE, "oppositeDirection" : true, "depth" : 4.5 * mm, "symmetric" : true});
        }
        {
            var Q0;
            Q0=qCreatedBy(makeId("Top.planeOp"),FACE);
            var sketch = newSketch(context, id + "F33", { "sketchPlane" : qUnion([Q0])});
            skCircle(sketch, "E66", {"center": v(0, 0) * mm, "radius": 1.5 * mm});
            skSolve(sketch);
        }
        {
            var Q0;
            Q0=makeQuery(id+"F33.imprint","IMPRINT",FACE,{"disambiguationData":[TD([[makeQuery(id+"F33.imprint","IMPRINT",EDGE,{"derivedFrom":sQuery(id+"F33.wireOp",EDGE,"E66")}),1.0]])]});
            extrude(context, id + "F34", {"entities" : qUnion([Q0]), "operationType" : NewBodyOperationType.REMOVE, "depth" : 11.5 * mm});
        }
        {
            var Q0;
            Q0=makeQuery(id+"F1.opExtrude","CAP_FACE",FACE,{"disambiguationData":[OSD([sQuery(id+"F0.wireOp",EDGE,"E0")])],"isStart":false});
            var sketch = newSketch(context, id + "F35", { "sketchPlane" : qUnion([Q0])});
            skLineSegment(sketch, "E67", {"start": v(0, 0) * mm, "end": v(0, 4) * mm, "construction": true});
            skCircle(sketch, "E68", {"center": v(0, 4) * mm, "radius": 9 * mm});
            skCircle(sketch, "E69", {"center": v(0, 4) * mm, "radius": 10.5 * mm});
            skSolve(sketch);
        }
        {
            var Q0;
            Q0=makeQuery(id+"F35.imprint","IMPRINT",FACE,{"disambiguationData":[TD([[makeQuery(id+"F35.imprint","IMPRINT",EDGE,{"derivedFrom":sQuery(id+"F35.wireOp",EDGE,"E68")}),1.0]])]});
            var Q1;
            Q1=makeQuery(id+"F35.imprint","IMPRINT",FACE,{"disambiguationData":[TD([[makeQuery(id+"F35.imprint","IMPRINT",EDGE,{"derivedFrom":sQuery(id+"F35.wireOp",EDGE,"E68")}),-1.0]])]});
            extrude(context, id + "F36", {"entities" : qUnion([Q0, Q1]), "depth" : 6 * mm, "symmetric" : true});
        }
        {
            var Q0;
            Q0=makeQuery(id+"F35.imprint","IMPRINT",FACE,{"disambiguationData":[TD([[makeQuery(id+"F35.imprint","IMPRINT",EDGE,{"derivedFrom":sQuery(id+"F35.wireOp",EDGE,"E68")}),-1.0]])]});
            extrude(context, id + "F37", {"entities" : qUnion([Q0]), "operationType" : NewBodyOperationType.REMOVE, "oppositeDirection" : true, "depth" : 5 * mm, "symmetric" : true});
        }
        {
            var Q0;
            Q0=qCreatedBy(makeId("Top.planeOp"),FACE);
            var sketch = newSketch(context, id + "F38", { "sketchPlane" : qUnion([Q0])});
            skLineSegment(sketch, "E70.0", {"start": v(-42.5, 4) * mm, "end": v(-42.5, -4) * mm});
            skLineSegment(sketch, "E70.1", {"start": v(-36.5, 4) * mm, "end": v(-36.5, -4) * mm});
            skLineSegment(sketch, "E71", {"start": v(-42.5, 0) * mm, "end": v(-36.5, 0) * mm, "construction": true});
            skCircle(sketch, "E72", {"center": v(-39.5, 0) * mm, "radius": 1.5 * mm});
            skSolve(sketch);
        }
        {
            var Q0;
            Q0=makeQuery(id+"F38.imprint","IMPRINT",FACE,{"disambiguationData":[TD([[makeQuery(id+"F38.imprint","IMPRINT",EDGE,{"derivedFrom":sQuery(id+"F38.wireOp",EDGE,"E72")}),1.0]])]});
            extrude(context, id + "F39", {"entities" : qUnion([Q0]), "operationType" : NewBodyOperationType.REMOVE, "depth" : 13 * mm});
        }
        {
            var Q0;
            Q0=makeQuery(id+"F29.opExtrude","CAP_FACE",FACE,{"disambiguationData":[OSD([sQuery(id+"F27.wireOp",EDGE,"E59"),sQuery(id+"F27.wireOp",EDGE,"E60")])],"isStart":false});
            var sketch = newSketch(context, id + "F40", { "sketchPlane" : qUnion([Q0])});
            skCircle(sketch, "E73", {"center": v(0, 0) * mm, "radius": 8.25 * mm});
            skCircle(sketch, "E74", {"center": v(0, 0) * mm, "radius": 10.75 * mm});
            skCircle(sketch, "E75", {"center": v(0, 0) * mm, "radius": 9.5 * mm, "construction": true});
            skLineSegment(sketch, "E76", {"start": v(0, 0) * mm, "end": v(0, 10.75) * mm, "construction": true});
            skLineSegment(sketch, "E77", {"start": v(0, 0) * mm, "end": v(-1, 9.45) * mm, "construction": true});
            skLineSegment(sketch, "E78", {"start": v(0, 8.25) * mm, "end": v(15, 8.25) * mm, "construction": true});
            skArc(sketch, "E79", {"start": v(-0.85, 10.72) * mm, "mid": v(-1, 9.45) * mm, "end": v(-1.04, 8.18) * mm});
            skArc(sketch, "E80.0.MirrorCS", {"start": v(0.85, 10.72) * mm, "mid": v(1, 9.45) * mm, "end": v(1.04, 8.18) * mm});
            skArc(sketch, "E81.1.0", {"start": v(-5.13, 9.45) * mm, "mid": v(-4.75, 8.23) * mm, "end": v(-4.28, 7.05) * mm});
            skArc(sketch, "E81.1.1", {"start": v(-3.59, 10.13) * mm, "mid": v(-2.94, 9.04) * mm, "end": v(-2.38, 7.9) * mm});
            skArc(sketch, "E81.2.0", {"start": v(-8.53, 6.54) * mm, "mid": v(-7.7, 5.59) * mm, "end": v(-6.78, 4.7) * mm});
            skArc(sketch, "E81.2.1", {"start": v(-7.4, 7.8) * mm, "mid": v(-6.36, 7.06) * mm, "end": v(-5.39, 6.25) * mm});
            skArc(sketch, "E81.3.0", {"start": v(-10.45, 2.5) * mm, "mid": v(-9.3, 1.98) * mm, "end": v(-8.1, 1.54) * mm});
            skArc(sketch, "E81.3.1", {"start": v(-9.93, 4.12) * mm, "mid": v(-8.68, 3.87) * mm, "end": v(-7.46, 3.52) * mm});
            skArc(sketch, "E81.4.0", {"start": v(-10.57, -1.96) * mm, "mid": v(-9.3, -1.98) * mm, "end": v(-8.03, -1.89) * mm});
            skArc(sketch, "E81.4.1", {"start": v(-10.75, -0.28) * mm, "mid": v(-9.5, 0) * mm, "end": v(-8.25, 0.18) * mm});
            skArc(sketch, "E81.5.0", {"start": v(-8.86, -6.1) * mm, "mid": v(-7.7, -5.59) * mm, "end": v(-6.57, -5) * mm});
            skArc(sketch, "E81.5.1", {"start": v(-9.7, -4.62) * mm, "mid": v(-8.68, -3.87) * mm, "end": v(-7.6, -3.2) * mm});
            skArc(sketch, "E81.6.0", {"start": v(-5.61, -9.17) * mm, "mid": v(-4.75, -8.23) * mm, "end": v(-3.97, -7.23) * mm});
            skArc(sketch, "E81.6.1", {"start": v(-6.98, -8.17) * mm, "mid": v(-6.36, -7.07) * mm, "end": v(-5.65, -6.01) * mm});
            skArc(sketch, "E81.7.0", {"start": v(-1.4, -10.66) * mm, "mid": v(-1, -9.45) * mm, "end": v(-0.69, -8.22) * mm});
            skArc(sketch, "E81.7.1", {"start": v(-3.06, -10.3) * mm, "mid": v(-2.94, -9.04) * mm, "end": v(-2.72, -7.79) * mm});
            skArc(sketch, "E81.8.0", {"start": v(3.06, -10.3) * mm, "mid": v(2.94, -9.04) * mm, "end": v(2.72, -7.79) * mm});
            skArc(sketch, "E81.8.1", {"start": v(1.4, -10.66) * mm, "mid": v(1, -9.45) * mm, "end": v(0.69, -8.22) * mm});
            skArc(sketch, "E81.9.0", {"start": v(6.98, -8.17) * mm, "mid": v(6.36, -7.07) * mm, "end": v(5.65, -6.01) * mm});
            skArc(sketch, "E81.9.1", {"start": v(5.61, -9.17) * mm, "mid": v(4.75, -8.23) * mm, "end": v(3.97, -7.23) * mm});
            skArc(sketch, "E81.10.0", {"start": v(9.7, -4.62) * mm, "mid": v(8.68, -3.87) * mm, "end": v(7.6, -3.2) * mm});
            skArc(sketch, "E81.10.1", {"start": v(8.86, -6.1) * mm, "mid": v(7.7, -5.59) * mm, "end": v(6.57, -5) * mm});
            skArc(sketch, "E81.11.0", {"start": v(10.75, -0.28) * mm, "mid": v(9.5, 0) * mm, "end": v(8.25, 0.18) * mm});
            skArc(sketch, "E81.11.1", {"start": v(10.57, -1.96) * mm, "mid": v(9.3, -1.98) * mm, "end": v(8.03, -1.89) * mm});
            skArc(sketch, "E81.12.0", {"start": v(9.93, 4.12) * mm, "mid": v(8.68, 3.87) * mm, "end": v(7.46, 3.52) * mm});
            skArc(sketch, "E81.12.1", {"start": v(10.45, 2.5) * mm, "mid": v(9.3, 1.98) * mm, "end": v(8.1, 1.54) * mm});
            skArc(sketch, "E81.13.0", {"start": v(7.4, 7.8) * mm, "mid": v(6.36, 7.06) * mm, "end": v(5.39, 6.25) * mm});
            skArc(sketch, "E81.13.1", {"start": v(8.53, 6.54) * mm, "mid": v(7.7, 5.59) * mm, "end": v(6.78, 4.7) * mm});
            skArc(sketch, "E81.14.0", {"start": v(3.59, 10.13) * mm, "mid": v(2.94, 9.04) * mm, "end": v(2.38, 7.9) * mm});
            skArc(sketch, "E81.14.1", {"start": v(5.13, 9.45) * mm, "mid": v(4.75, 8.23) * mm, "end": v(4.28, 7.05) * mm});
            skSolve(sketch);
        }
        {
            var Q0;
            Q0=makeQuery(id+"F40.imprint","IMPRINT",FACE,{"disambiguationData":[TD([[makeQuery(id+"F40.imprint","IMPRINT",EDGE,{"derivedFrom":makeQuery(id+"F29.opExtrude","CAP_EDGE",EDGE,{"disambiguationData":[OSD([sQuery(id+"F27.wireOp",EDGE,"E60")])],"isStart":false})}),-1.0]])]});
            var Q1;
            Q1=makeQuery(id+"F40.imprint","IMPRINT",FACE,{"disambiguationData":[TD([[makeQuery(id+"F40.imprint","IMPRINT",EDGE,{"derivedFrom":makeQuery(id+"F29.opExtrude","CAP_EDGE",EDGE,{"disambiguationData":[OSD([sQuery(id+"F27.wireOp",EDGE,"E60")])],"isStart":false})}),1.0]])]});
            var Q2;
            {var subQ1=sQuery(id+"F40.wireOp",EDGE,"E81.1.0");Q2=makeQuery(id+"F40.imprint","IMPRINT",FACE,{"disambiguationData":[TD([[makeQuery(id+"F40.imprint","IMPRINT",EDGE,{"derivedFrom":subQ1}),1.0]])]});}
            var Q3;
            {var subQ1=sQuery(id+"F40.wireOp",EDGE,"E79");Q3=makeQuery(id+"F40.imprint","IMPRINT",FACE,{"disambiguationData":[TD([[makeQuery(id+"F40.imprint","IMPRINT",EDGE,{"derivedFrom":subQ1}),1.0]])]});}
            var Q4;
            {var subQ1=sQuery(id+"F40.wireOp",EDGE,"E81.14.0");Q4=makeQuery(id+"F40.imprint","IMPRINT",FACE,{"disambiguationData":[TD([[makeQuery(id+"F40.imprint","IMPRINT",EDGE,{"derivedFrom":subQ1}),1.0]])]});}
            var Q5;
            {var subQ1=sQuery(id+"F40.wireOp",EDGE,"E81.13.0");Q5=makeQuery(id+"F40.imprint","IMPRINT",FACE,{"disambiguationData":[TD([[makeQuery(id+"F40.imprint","IMPRINT",EDGE,{"derivedFrom":subQ1}),1.0]])]});}
            var Q6;
            {var subQ1=sQuery(id+"F40.wireOp",EDGE,"E81.12.0");Q6=makeQuery(id+"F40.imprint","IMPRINT",FACE,{"disambiguationData":[TD([[makeQuery(id+"F40.imprint","IMPRINT",EDGE,{"derivedFrom":subQ1}),1.0]])]});}
            var Q7;
            {var subQ1=sQuery(id+"F40.wireOp",EDGE,"E81.11.0");Q7=makeQuery(id+"F40.imprint","IMPRINT",FACE,{"disambiguationData":[TD([[makeQuery(id+"F40.imprint","IMPRINT",EDGE,{"derivedFrom":subQ1}),1.0]])]});}
            var Q8;
            {var subQ1=sQuery(id+"F40.wireOp",EDGE,"E81.10.0");Q8=makeQuery(id+"F40.imprint","IMPRINT",FACE,{"disambiguationData":[TD([[makeQuery(id+"F40.imprint","IMPRINT",EDGE,{"derivedFrom":subQ1}),1.0]])]});}
            var Q9;
            {var subQ1=sQuery(id+"F40.wireOp",EDGE,"E81.9.0");Q9=makeQuery(id+"F40.imprint","IMPRINT",FACE,{"disambiguationData":[TD([[makeQuery(id+"F40.imprint","IMPRINT",EDGE,{"derivedFrom":subQ1}),1.0]])]});}
            var Q10;
            {var subQ1=sQuery(id+"F40.wireOp",EDGE,"E81.8.0");Q10=makeQuery(id+"F40.imprint","IMPRINT",FACE,{"disambiguationData":[TD([[makeQuery(id+"F40.imprint","IMPRINT",EDGE,{"derivedFrom":subQ1}),1.0]])]});}
            var Q11;
            {var subQ1=sQuery(id+"F40.wireOp",EDGE,"E81.7.0");Q11=makeQuery(id+"F40.imprint","IMPRINT",FACE,{"disambiguationData":[TD([[makeQuery(id+"F40.imprint","IMPRINT",EDGE,{"derivedFrom":subQ1}),1.0]])]});}
            var Q12;
            {var subQ1=sQuery(id+"F40.wireOp",EDGE,"E81.6.0");Q12=makeQuery(id+"F40.imprint","IMPRINT",FACE,{"disambiguationData":[TD([[makeQuery(id+"F40.imprint","IMPRINT",EDGE,{"derivedFrom":subQ1}),1.0]])]});}
            var Q13;
            {var subQ1=sQuery(id+"F40.wireOp",EDGE,"E81.5.0");Q13=makeQuery(id+"F40.imprint","IMPRINT",FACE,{"disambiguationData":[TD([[makeQuery(id+"F40.imprint","IMPRINT",EDGE,{"derivedFrom":subQ1}),1.0]])]});}
            var Q14;
            {var subQ1=sQuery(id+"F40.wireOp",EDGE,"E81.4.0");Q14=makeQuery(id+"F40.imprint","IMPRINT",FACE,{"disambiguationData":[TD([[makeQuery(id+"F40.imprint","IMPRINT",EDGE,{"derivedFrom":subQ1}),1.0]])]});}
            var Q15;
            {var subQ1=sQuery(id+"F40.wireOp",EDGE,"E81.3.0");Q15=makeQuery(id+"F40.imprint","IMPRINT",FACE,{"disambiguationData":[TD([[makeQuery(id+"F40.imprint","IMPRINT",EDGE,{"derivedFrom":subQ1}),1.0]])]});}
            var Q16;
            {var subQ1=sQuery(id+"F40.wireOp",EDGE,"E81.2.0");Q16=makeQuery(id+"F40.imprint","IMPRINT",FACE,{"disambiguationData":[TD([[makeQuery(id+"F40.imprint","IMPRINT",EDGE,{"derivedFrom":subQ1}),1.0]])]});}
            extrude(context, id + "F41", {"entities" : qUnion([Q0, Q1, Q2, Q3, Q4, Q5, Q6, Q7, Q8, Q9, Q10, Q11, Q12, Q13, Q14, Q15, Q16]), "depth" : 4 * mm});
        }
        {
            var Q0;
            Q0=qCreatedBy(makeId("Front.planeOp"),FACE);
            var sketch = newSketch(context, id + "F42", { "sketchPlane" : qUnion([Q0])});
            skLineSegment(sketch, "E82.0", {"start": v(40.8, 8.25) * mm, "end": v(40.8, -8.25) * mm});
            skLineSegment(sketch, "E82.1", {"start": v(40.8, 9.5) * mm, "end": v(40.8, -9.5) * mm});
            skLineSegment(sketch, "E82.2", {"start": v(40.8, 10.75) * mm, "end": v(40.8, -10.75) * mm});
            skLineSegment(sketch, "E83.bottom", {"start": v(40.8, 8.25) * mm, "end": v(44.8, 8.25) * mm});
            skLineSegment(sketch, "E83.top", {"start": v(40.8, 10.75) * mm, "end": v(44.8, 10.75) * mm});
            skLineSegment(sketch, "E83.left", {"start": v(40.8, 8.25) * mm, "end": v(40.8, 10.75) * mm});
            skLineSegment(sketch, "E83.right", {"start": v(44.8, 8.25) * mm, "end": v(44.8, 10.75) * mm});
            skLineSegment(sketch, "E84", {"start": v(42.8, 10.75) * mm, "end": v(42.8, 8.25) * mm, "construction": true});
            skLineSegment(sketch, "E85", {"start": v(40.8, 8.25) * mm, "end": v(50.8, 8.25) * mm, "construction": true});
            skLineSegment(sketch, "E86", {"start": v(40.8, 0) * mm, "end": v(46.26, 0) * mm, "construction": true});
            skArc(sketch, "E87", {"start": v(41.04, 10.75) * mm, "mid": v(40.9, 10.13) * mm, "end": v(40.8, 9.5) * mm});
            skArc(sketch, "E88.0.MirrorCS", {"start": v(44.56, 10.75) * mm, "mid": v(44.7, 10.13) * mm, "end": v(44.8, 9.5) * mm});
            skSolve(sketch);
        }
        {
            var Q0;
            {var subQ0=sQuery(id+"F42.wireOp",EDGE,"E87");Q0=makeQuery(id+"F42.imprint","IMPRINT",FACE,{"disambiguationData":[TD([[makeQuery(id+"F42.imprint","IMPRINT",EDGE,{"derivedFrom":subQ0}),-1.0]])]});}
            var Q1;
            {var subQ0=sQuery(id+"F42.wireOp",EDGE,"E88.0.MirrorCS");Q1=makeQuery(id+"F42.imprint","IMPRINT",FACE,{"disambiguationData":[TD([[makeQuery(id+"F42.imprint","IMPRINT",EDGE,{"derivedFrom":subQ0}),1.0]])]});}
            var Q2;
            Q2=sQuery(id+"F42.wireOp",EDGE,"E86");
            revolve(context, id + "F43", {"operationType" : NewBodyOperationType.REMOVE, "entities" : qUnion([Q0, Q1]), "axis" : qUnion([Q2]), "revolveType" : RevolveType.FULL, "oppositeDirection" : true});
        }
        {
            var Q0;
            Q0=makeQuery(id+"F29.opExtrude","CAP_FACE",FACE,{"disambiguationData":[OSD([sQuery(id+"F27.wireOp",EDGE,"E59"),sQuery(id+"F27.wireOp",EDGE,"E60")])],"isStart":true});
            var sketch = newSketch(context, id + "F44", { "sketchPlane" : qUnion([Q0])});
            skCircle(sketch, "E89", {"center": v(0, 0) * mm, "radius": 11.5 * mm});
            skCircle(sketch, "E90", {"center": v(0, 0) * mm, "radius": 14 * mm});
            skCircle(sketch, "E91", {"center": v(0, 0) * mm, "radius": 12.75 * mm, "construction": true});
            skLineSegment(sketch, "E92", {"start": v(0, 0) * mm, "end": v(0, 14) * mm, "construction": true});
            skLineSegment(sketch, "E93", {"start": v(0, 0) * mm, "end": v(-1, 12.71) * mm, "construction": true});
            skLineSegment(sketch, "E94", {"start": v(0, 11.5) * mm, "end": v(15, 11.5) * mm, "construction": true});
            skArc(sketch, "E95", {"start": v(-0.85, 13.97) * mm, "mid": v(-1, 12.72) * mm, "end": v(-1.05, 11.45) * mm});
            skArc(sketch, "E96.0.MirrorCS", {"start": v(0.85, 13.97) * mm, "mid": v(1, 12.72) * mm, "end": v(1.05, 11.45) * mm});
            skArc(sketch, "E97.1.0", {"start": v(-5.13, 13.03) * mm, "mid": v(-4.88, 11.79) * mm, "end": v(-4.53, 10.57) * mm});
            skArc(sketch, "E97.1.1", {"start": v(-3.5, 13.55) * mm, "mid": v(-2.98, 12.4) * mm, "end": v(-2.54, 11.22) * mm});
            skArc(sketch, "E97.2.0", {"start": v(-8.9, 10.8) * mm, "mid": v(-8.28, 9.7) * mm, "end": v(-7.58, 8.65) * mm});
            skArc(sketch, "E97.2.1", {"start": v(-7.52, 11.8) * mm, "mid": v(-6.67, 10.88) * mm, "end": v(-5.89, 9.88) * mm});
            skArc(sketch, "E97.3.0", {"start": v(-11.8, 7.52) * mm, "mid": v(-10.88, 6.67) * mm, "end": v(-9.88, 5.89) * mm});
            skArc(sketch, "E97.3.1", {"start": v(-10.8, 8.9) * mm, "mid": v(-9.7, 8.28) * mm, "end": v(-8.65, 7.58) * mm});
            skArc(sketch, "E97.4.0", {"start": v(-13.55, 3.5) * mm, "mid": v(-12.4, 2.98) * mm, "end": v(-11.22, 2.54) * mm});
            skArc(sketch, "E97.4.1", {"start": v(-13.03, 5.13) * mm, "mid": v(-11.79, 4.88) * mm, "end": v(-10.57, 4.53) * mm});
            skArc(sketch, "E97.5.0", {"start": v(-13.97, -0.85) * mm, "mid": v(-12.72, -1) * mm, "end": v(-11.45, -1.05) * mm});
            skArc(sketch, "E97.5.1", {"start": v(-13.97, 0.85) * mm, "mid": v(-12.72, 1) * mm, "end": v(-11.45, 1.05) * mm});
            skArc(sketch, "E97.6.0", {"start": v(-13.03, -5.13) * mm, "mid": v(-11.79, -4.88) * mm, "end": v(-10.57, -4.53) * mm});
            skArc(sketch, "E97.6.1", {"start": v(-13.55, -3.5) * mm, "mid": v(-12.4, -2.98) * mm, "end": v(-11.22, -2.54) * mm});
            skArc(sketch, "E97.7.0", {"start": v(-10.8, -8.9) * mm, "mid": v(-9.7, -8.28) * mm, "end": v(-8.65, -7.58) * mm});
            skArc(sketch, "E97.7.1", {"start": v(-11.8, -7.52) * mm, "mid": v(-10.88, -6.67) * mm, "end": v(-9.88, -5.89) * mm});
            skArc(sketch, "E97.8.0", {"start": v(-7.52, -11.8) * mm, "mid": v(-6.67, -10.88) * mm, "end": v(-5.89, -9.88) * mm});
            skArc(sketch, "E97.8.1", {"start": v(-8.9, -10.8) * mm, "mid": v(-8.28, -9.7) * mm, "end": v(-7.58, -8.65) * mm});
            skArc(sketch, "E97.9.0", {"start": v(-3.5, -13.55) * mm, "mid": v(-2.98, -12.4) * mm, "end": v(-2.54, -11.22) * mm});
            skArc(sketch, "E97.9.1", {"start": v(-5.13, -13.03) * mm, "mid": v(-4.88, -11.79) * mm, "end": v(-4.53, -10.57) * mm});
            skArc(sketch, "E97.10.0", {"start": v(0.85, -13.97) * mm, "mid": v(1, -12.72) * mm, "end": v(1.05, -11.45) * mm});
            skArc(sketch, "E97.10.1", {"start": v(-0.85, -13.97) * mm, "mid": v(-1, -12.72) * mm, "end": v(-1.05, -11.45) * mm});
            skArc(sketch, "E97.11.0", {"start": v(5.13, -13.03) * mm, "mid": v(4.88, -11.79) * mm, "end": v(4.53, -10.57) * mm});
            skArc(sketch, "E97.11.1", {"start": v(3.5, -13.55) * mm, "mid": v(2.98, -12.4) * mm, "end": v(2.54, -11.22) * mm});
            skArc(sketch, "E97.12.0", {"start": v(8.9, -10.8) * mm, "mid": v(8.28, -9.7) * mm, "end": v(7.58, -8.65) * mm});
            skArc(sketch, "E97.12.1", {"start": v(7.52, -11.8) * mm, "mid": v(6.67, -10.88) * mm, "end": v(5.89, -9.88) * mm});
            skArc(sketch, "E97.13.0", {"start": v(11.8, -7.52) * mm, "mid": v(10.88, -6.67) * mm, "end": v(9.88, -5.89) * mm});
            skArc(sketch, "E97.13.1", {"start": v(10.8, -8.9) * mm, "mid": v(9.7, -8.28) * mm, "end": v(8.65, -7.58) * mm});
            skArc(sketch, "E97.14.0", {"start": v(13.55, -3.5) * mm, "mid": v(12.4, -2.98) * mm, "end": v(11.22, -2.54) * mm});
            skArc(sketch, "E97.14.1", {"start": v(13.03, -5.13) * mm, "mid": v(11.79, -4.88) * mm, "end": v(10.57, -4.53) * mm});
            skArc(sketch, "E97.15.0", {"start": v(13.97, 0.85) * mm, "mid": v(12.72, 1) * mm, "end": v(11.45, 1.05) * mm});
            skArc(sketch, "E97.15.1", {"start": v(13.97, -0.85) * mm, "mid": v(12.72, -1) * mm, "end": v(11.45, -1.05) * mm});
            skArc(sketch, "E97.16.0", {"start": v(13.03, 5.13) * mm, "mid": v(11.79, 4.88) * mm, "end": v(10.57, 4.53) * mm});
            skArc(sketch, "E97.16.1", {"start": v(13.55, 3.5) * mm, "mid": v(12.4, 2.98) * mm, "end": v(11.22, 2.54) * mm});
            skArc(sketch, "E97.17.0", {"start": v(10.8, 8.9) * mm, "mid": v(9.7, 8.28) * mm, "end": v(8.65, 7.58) * mm});
            skArc(sketch, "E97.17.1", {"start": v(11.8, 7.52) * mm, "mid": v(10.88, 6.67) * mm, "end": v(9.88, 5.89) * mm});
            skArc(sketch, "E97.18.0", {"start": v(7.52, 11.8) * mm, "mid": v(6.67, 10.88) * mm, "end": v(5.89, 9.88) * mm});
            skArc(sketch, "E97.18.1", {"start": v(8.9, 10.8) * mm, "mid": v(8.28, 9.7) * mm, "end": v(7.58, 8.65) * mm});
            skArc(sketch, "E97.19.0", {"start": v(3.5, 13.55) * mm, "mid": v(2.98, 12.4) * mm, "end": v(2.54, 11.22) * mm});
            skArc(sketch, "E97.19.1", {"start": v(5.13, 13.03) * mm, "mid": v(4.88, 11.79) * mm, "end": v(4.53, 10.57) * mm});
            skSolve(sketch);
        }
        {
            var Q0;
            Q0=makeQuery(id+"F44.imprint","IMPRINT",FACE,{"disambiguationData":[TD([[makeQuery(id+"F44.imprint","IMPRINT",EDGE,{"derivedFrom":makeQuery(id+"F29.opExtrude","CAP_EDGE",EDGE,{"disambiguationData":[OSD([sQuery(id+"F27.wireOp",EDGE,"E60")])],"isStart":true})}),-1.0]])]});
            var Q1;
            Q1=makeQuery(id+"F44.imprint","IMPRINT",FACE,{"disambiguationData":[TD([[makeQuery(id+"F44.imprint","IMPRINT",EDGE,{"derivedFrom":makeQuery(id+"F29.opExtrude","CAP_EDGE",EDGE,{"disambiguationData":[OSD([sQuery(id+"F27.wireOp",EDGE,"E60")])],"isStart":true})}),1.0]])]});
            var Q2;
            {var subQ1=sQuery(id+"F44.wireOp",EDGE,"E95");Q2=makeQuery(id+"F44.imprint","IMPRINT",FACE,{"disambiguationData":[TD([[makeQuery(id+"F44.imprint","IMPRINT",EDGE,{"derivedFrom":subQ1}),1.0]])]});}
            var Q3;
            {var subQ1=sQuery(id+"F44.wireOp",EDGE,"E97.19.0");Q3=makeQuery(id+"F44.imprint","IMPRINT",FACE,{"disambiguationData":[TD([[makeQuery(id+"F44.imprint","IMPRINT",EDGE,{"derivedFrom":subQ1}),1.0]])]});}
            var Q4;
            {var subQ1=sQuery(id+"F44.wireOp",EDGE,"E97.18.0");Q4=makeQuery(id+"F44.imprint","IMPRINT",FACE,{"disambiguationData":[TD([[makeQuery(id+"F44.imprint","IMPRINT",EDGE,{"derivedFrom":subQ1}),1.0]])]});}
            var Q5;
            {var subQ1=sQuery(id+"F44.wireOp",EDGE,"E97.17.0");Q5=makeQuery(id+"F44.imprint","IMPRINT",FACE,{"disambiguationData":[TD([[makeQuery(id+"F44.imprint","IMPRINT",EDGE,{"derivedFrom":subQ1}),1.0]])]});}
            var Q6;
            {var subQ1=sQuery(id+"F44.wireOp",EDGE,"E97.16.0");Q6=makeQuery(id+"F44.imprint","IMPRINT",FACE,{"disambiguationData":[TD([[makeQuery(id+"F44.imprint","IMPRINT",EDGE,{"derivedFrom":subQ1}),1.0]])]});}
            var Q7;
            {var subQ1=sQuery(id+"F44.wireOp",EDGE,"E97.15.0");Q7=makeQuery(id+"F44.imprint","IMPRINT",FACE,{"disambiguationData":[TD([[makeQuery(id+"F44.imprint","IMPRINT",EDGE,{"derivedFrom":subQ1}),1.0]])]});}
            var Q8;
            {var subQ1=sQuery(id+"F44.wireOp",EDGE,"E97.14.0");Q8=makeQuery(id+"F44.imprint","IMPRINT",FACE,{"disambiguationData":[TD([[makeQuery(id+"F44.imprint","IMPRINT",EDGE,{"derivedFrom":subQ1}),1.0]])]});}
            var Q9;
            {var subQ1=sQuery(id+"F44.wireOp",EDGE,"E97.13.0");Q9=makeQuery(id+"F44.imprint","IMPRINT",FACE,{"disambiguationData":[TD([[makeQuery(id+"F44.imprint","IMPRINT",EDGE,{"derivedFrom":subQ1}),1.0]])]});}
            var Q10;
            {var subQ1=sQuery(id+"F44.wireOp",EDGE,"E97.12.0");Q10=makeQuery(id+"F44.imprint","IMPRINT",FACE,{"disambiguationData":[TD([[makeQuery(id+"F44.imprint","IMPRINT",EDGE,{"derivedFrom":subQ1}),1.0]])]});}
            var Q11;
            {var subQ1=sQuery(id+"F44.wireOp",EDGE,"E97.11.0");Q11=makeQuery(id+"F44.imprint","IMPRINT",FACE,{"disambiguationData":[TD([[makeQuery(id+"F44.imprint","IMPRINT",EDGE,{"derivedFrom":subQ1}),1.0]])]});}
            var Q12;
            {var subQ1=sQuery(id+"F44.wireOp",EDGE,"E97.10.0");Q12=makeQuery(id+"F44.imprint","IMPRINT",FACE,{"disambiguationData":[TD([[makeQuery(id+"F44.imprint","IMPRINT",EDGE,{"derivedFrom":subQ1}),1.0]])]});}
            var Q13;
            {var subQ1=sQuery(id+"F44.wireOp",EDGE,"E97.9.0");Q13=makeQuery(id+"F44.imprint","IMPRINT",FACE,{"disambiguationData":[TD([[makeQuery(id+"F44.imprint","IMPRINT",EDGE,{"derivedFrom":subQ1}),1.0]])]});}
            var Q14;
            {var subQ1=sQuery(id+"F44.wireOp",EDGE,"E97.8.0");Q14=makeQuery(id+"F44.imprint","IMPRINT",FACE,{"disambiguationData":[TD([[makeQuery(id+"F44.imprint","IMPRINT",EDGE,{"derivedFrom":subQ1}),1.0]])]});}
            var Q15;
            {var subQ2=sQuery(id+"F44.wireOp",EDGE,"E97.7.0");Q15=makeQuery(id+"F44.imprint","IMPRINT",FACE,{"disambiguationData":[TD([[makeQuery(id+"F44.imprint","IMPRINT",EDGE,{"derivedFrom":subQ2}),1.0]])]});}
            var Q16;
            {var subQ1=sQuery(id+"F44.wireOp",EDGE,"E97.6.0");Q16=makeQuery(id+"F44.imprint","IMPRINT",FACE,{"disambiguationData":[TD([[makeQuery(id+"F44.imprint","IMPRINT",EDGE,{"derivedFrom":subQ1}),1.0]])]});}
            var Q17;
            {var subQ1=sQuery(id+"F44.wireOp",EDGE,"E97.5.0");Q17=makeQuery(id+"F44.imprint","IMPRINT",FACE,{"disambiguationData":[TD([[makeQuery(id+"F44.imprint","IMPRINT",EDGE,{"derivedFrom":subQ1}),1.0]])]});}
            var Q18;
            {var subQ1=sQuery(id+"F44.wireOp",EDGE,"E97.4.0");Q18=makeQuery(id+"F44.imprint","IMPRINT",FACE,{"disambiguationData":[TD([[makeQuery(id+"F44.imprint","IMPRINT",EDGE,{"derivedFrom":subQ1}),1.0]])]});}
            var Q19;
            {var subQ1=sQuery(id+"F44.wireOp",EDGE,"E97.3.0");Q19=makeQuery(id+"F44.imprint","IMPRINT",FACE,{"disambiguationData":[TD([[makeQuery(id+"F44.imprint","IMPRINT",EDGE,{"derivedFrom":subQ1}),1.0]])]});}
            var Q20;
            {var subQ1=sQuery(id+"F44.wireOp",EDGE,"E97.2.0");Q20=makeQuery(id+"F44.imprint","IMPRINT",FACE,{"disambiguationData":[TD([[makeQuery(id+"F44.imprint","IMPRINT",EDGE,{"derivedFrom":subQ1}),1.0]])]});}
            var Q21;
            {var subQ1=sQuery(id+"F44.wireOp",EDGE,"E97.1.0");Q21=makeQuery(id+"F44.imprint","IMPRINT",FACE,{"disambiguationData":[TD([[makeQuery(id+"F44.imprint","IMPRINT",EDGE,{"derivedFrom":subQ1}),1.0]])]});}
            extrude(context, id + "F45", {"entities" : qUnion([Q0, Q1, Q2, Q3, Q4, Q5, Q6, Q7, Q8, Q9, Q10, Q11, Q12, Q13, Q14, Q15, Q16, Q17, Q18, Q19, Q20, Q21]), "depth" : 4 * mm});
        }
        {
            var Q0;
            Q0=qCreatedBy(makeId("Front.planeOp"),FACE);
            var sketch = newSketch(context, id + "F46", { "sketchPlane" : qUnion([Q0])});
            skLineSegment(sketch, "E98.0", {"start": v(29.8, -11.5) * mm, "end": v(29.8, 11.5) * mm});
            skLineSegment(sketch, "E98.1", {"start": v(29.8, -12.75) * mm, "end": v(29.8, 12.75) * mm});
            skLineSegment(sketch, "E98.2", {"start": v(29.8, -14) * mm, "end": v(29.8, 14) * mm});
            skLineSegment(sketch, "E99.bottom", {"start": v(29.8, 14) * mm, "end": v(25.8, 14) * mm});
            skLineSegment(sketch, "E99.top", {"start": v(29.8, 11.5) * mm, "end": v(25.8, 11.5) * mm});
            skLineSegment(sketch, "E99.left", {"start": v(29.8, 14) * mm, "end": v(29.8, 11.5) * mm});
            skLineSegment(sketch, "E99.right", {"start": v(25.8, 14) * mm, "end": v(25.8, 11.5) * mm});
            skLineSegment(sketch, "E100", {"start": v(27.8, 14) * mm, "end": v(27.8, 11.5) * mm, "construction": true});
            skLineSegment(sketch, "E101", {"start": v(29.8, 11.5) * mm, "end": v(19.8, 11.5) * mm, "construction": true});
            skLineSegment(sketch, "E102", {"start": v(29.8, 0) * mm, "end": v(24.27, 0) * mm, "construction": true});
            skArc(sketch, "E103", {"start": v(29.8, 12.75) * mm, "mid": v(29.7, 13.38) * mm, "end": v(29.56, 14) * mm});
            skArc(sketch, "E104.0.MirrorCS", {"start": v(25.8, 12.75) * mm, "mid": v(25.9, 13.38) * mm, "end": v(26.04, 14) * mm});
            skSolve(sketch);
        }
        {
            var Q0;
            {var subQ0=sQuery(id+"F46.wireOp",EDGE,"E104.0.MirrorCS");Q0=makeQuery(id+"F46.imprint","IMPRINT",FACE,{"disambiguationData":[TD([[makeQuery(id+"F46.imprint","IMPRINT",EDGE,{"derivedFrom":subQ0}),1.0]])]});}
            var Q1;
            {var subQ0=sQuery(id+"F46.wireOp",EDGE,"E103");Q1=makeQuery(id+"F46.imprint","IMPRINT",FACE,{"disambiguationData":[TD([[makeQuery(id+"F46.imprint","IMPRINT",EDGE,{"derivedFrom":subQ0}),-1.0]])]});}
            var Q2;
            Q2=sQuery(id+"F46.wireOp",EDGE,"E102");
            revolve(context, id + "F47", {"operationType" : NewBodyOperationType.REMOVE, "entities" : qUnion([Q0, Q1]), "axis" : qUnion([Q2]), "revolveType" : RevolveType.FULL, "oppositeDirection" : true});
        }
    });
